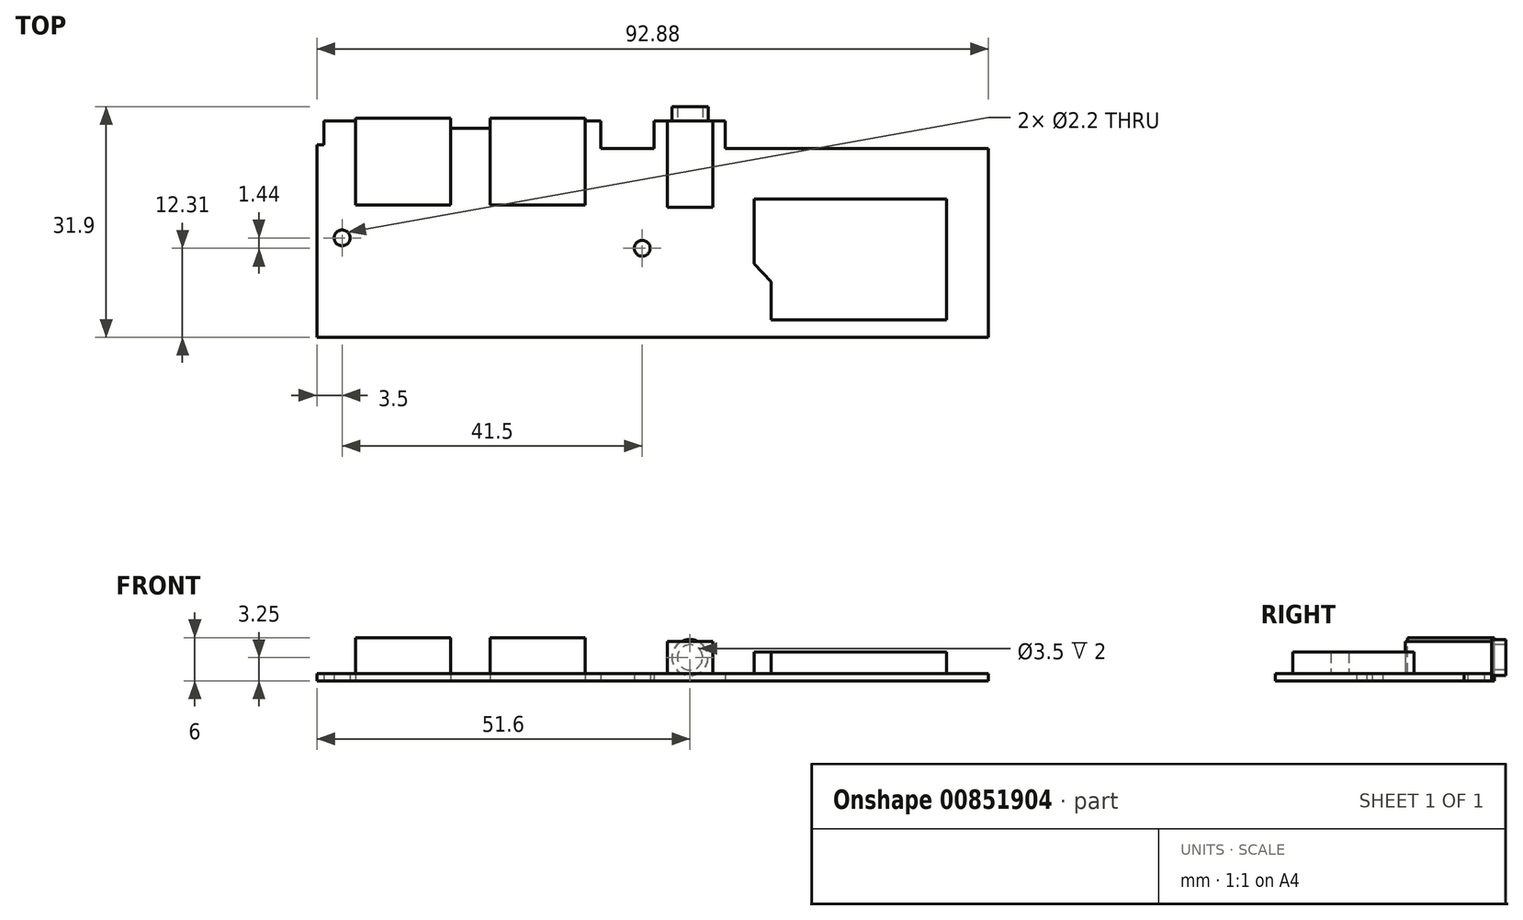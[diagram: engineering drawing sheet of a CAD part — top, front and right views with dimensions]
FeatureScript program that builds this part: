
annotation { "Feature Type Name" : "Feature", "Feature Type Description" : "" }
export const myFeature = defineFeature(function(context is Context, id is Id, definition is map)
    precondition{}
    {
        {
            var Q0;
            Q0=qCreatedBy(makeId("Top.planeOp"),FACE);
            var sketch = newSketch(context, id + "F0", { "sketchPlane" : qUnion([Q0])});
            skCircle(sketch, "E0", {"center": v(3.5, 13.75) * mm, "radius": 1.1 * mm});
            skCircle(sketch, "E1", {"center": v(45, 12.31) * mm, "radius": 1.1 * mm});
            skLineSegment(sketch, "E2", {"start": v(92.88, 26.1) * mm, "end": v(92.88, 0) * mm});
            skLineSegment(sketch, "E3", {"start": v(0, 0) * mm, "end": v(0, 26.6) * mm});
            skLineSegment(sketch, "E4", {"start": v(0, 26.6) * mm, "end": v(0.95, 26.6) * mm});
            skLineSegment(sketch, "E5", {"start": v(0.95, 26.6) * mm, "end": v(0.95, 29.9) * mm});
            skLineSegment(sketch, "E6", {"start": v(0.95, 29.9) * mm, "end": v(5.38, 29.9) * mm});
            skLineSegment(sketch, "E7", {"start": v(5.38, 29.9) * mm, "end": v(5.38, 18.3) * mm});
            skLineSegment(sketch, "E8", {"start": v(5.38, 18.3) * mm, "end": v(18.5, 18.3) * mm});
            skLineSegment(sketch, "E9", {"start": v(18.5, 18.3) * mm, "end": v(18.5, 28.9) * mm});
            skLineSegment(sketch, "E10", {"start": v(18.5, 28.9) * mm, "end": v(23.99, 28.9) * mm});
            skLineSegment(sketch, "E11", {"start": v(23.99, 28.9) * mm, "end": v(23.99, 18.3) * mm});
            skLineSegment(sketch, "E12", {"start": v(23.99, 18.3) * mm, "end": v(37.1, 18.3) * mm});
            skLineSegment(sketch, "E13", {"start": v(37.11, 18.3) * mm, "end": v(37.11, 29.9) * mm});
            skLineSegment(sketch, "E14", {"start": v(37.1, 29.9) * mm, "end": v(39.26, 29.9) * mm});
            skLineSegment(sketch, "E15", {"start": v(39.26, 29.9) * mm, "end": v(39.26, 26.1) * mm});
            skLineSegment(sketch, "E16", {"start": v(39.26, 26.1) * mm, "end": v(46.66, 26.1) * mm});
            skLineSegment(sketch, "E17", {"start": v(46.66, 26.1) * mm, "end": v(46.66, 29.9) * mm});
            skLineSegment(sketch, "E18", {"start": v(56.46, 29.9) * mm, "end": v(56.46, 26.1) * mm});
            skLineSegment(sketch, "E19", {"start": v(56.46, 26.1) * mm, "end": v(92.88, 26.1) * mm});
            skLineSegment(sketch, "E20", {"start": v(0, 0) * mm, "end": v(92.88, 0) * mm});
            skPoint(sketch, "E21", {"position": v(11.94, 18.3) * mm});
            skPoint(sketch, "E22", {"position": v(30.55, 18.3) * mm});
            skLineSegment(sketch, "E23", {"start": v(46.66, 29.9) * mm, "end": v(56.46, 29.9) * mm});
            skSolve(sketch);
        }
        {
            var Q0;
            Q0=makeQuery(id+"F0.imprint","IMPRINT",FACE,{"disambiguationData":[TD([[makeQuery(id+"F0.imprint","IMPRINT",EDGE,{"derivedFrom":sQuery(id+"F0.wireOp",EDGE,"E0")}),-1.0]])]});
            extrude(context, id + "F1", {"entities" : qUnion([Q0]), "depth" : 1 * mm, "offsetDistance" : 25 * mm});
        }
        {
            var Q0;
            Q0=makeQuery(id+"F1.opExtrude","CAP_FACE",FACE,{"disambiguationData":[OSD([sQuery(id+"F0.wireOp",EDGE,"E0"),sQuery(id+"F0.wireOp",EDGE,"E1"),sQuery(id+"F0.wireOp",EDGE,"E2"),sQuery(id+"F0.wireOp",EDGE,"E3"),sQuery(id+"F0.wireOp",EDGE,"E4"),sQuery(id+"F0.wireOp",EDGE,"E5"),sQuery(id+"F0.wireOp",EDGE,"E6"),sQuery(id+"F0.wireOp",EDGE,"E7"),sQuery(id+"F0.wireOp",EDGE,"E8"),sQuery(id+"F0.wireOp",EDGE,"E9"),sQuery(id+"F0.wireOp",EDGE,"E10"),sQuery(id+"F0.wireOp",EDGE,"E11"),sQuery(id+"F0.wireOp",EDGE,"E12"),sQuery(id+"F0.wireOp",EDGE,"E13"),sQuery(id+"F0.wireOp",EDGE,"E14"),sQuery(id+"F0.wireOp",EDGE,"E15"),sQuery(id+"F0.wireOp",EDGE,"E16"),sQuery(id+"F0.wireOp",EDGE,"E17"),sQuery(id+"F0.wireOp",EDGE,"E18"),sQuery(id+"F0.wireOp",EDGE,"E19"),sQuery(id+"F0.wireOp",EDGE,"E20"),sQuery(id+"F0.wireOp",EDGE,"E23")])],"isStart":false});
            var sketch = newSketch(context, id + "F2", { "sketchPlane" : qUnion([Q0])});
            skPoint(sketch, "E24.middle", {"position": v(51.6, 23.93) * mm});
            skLineSegment(sketch, "E25", {"start": v(87.1, 19.15) * mm, "end": v(87.1, 2.4) * mm});
            skLineSegment(sketch, "E26", {"start": v(87.1, 2.4) * mm, "end": v(62.8, 2.4) * mm});
            skLineSegment(sketch, "E27", {"start": v(62.8, 2.4) * mm, "end": v(62.8, 7.7) * mm});
            skLineSegment(sketch, "E28.bottom", {"start": v(54.75, 17.95) * mm, "end": v(48.45, 17.95) * mm});
            skLineSegment(sketch, "E28.top", {"start": v(54.75, 29.9) * mm, "end": v(48.45, 29.9) * mm});
            skLineSegment(sketch, "E28.left", {"start": v(54.75, 17.95) * mm, "end": v(54.75, 29.9) * mm});
            skLineSegment(sketch, "E28.right", {"start": v(48.45, 17.95) * mm, "end": v(48.45, 29.9) * mm});
            skLineSegment(sketch, "E29", {"start": v(87.1, 19.15) * mm, "end": v(60.5, 19.15) * mm});
            skLineSegment(sketch, "E30", {"start": v(60.5, 19.15) * mm, "end": v(60.5, 10.15) * mm});
            skLineSegment(sketch, "E31", {"start": v(60.5, 10.15) * mm, "end": v(62.8, 7.7) * mm});
            skSolve(sketch);
        }
        {
            var Q0;
            Q0=makeQuery(id+"F2.imprint","IMPRINT",FACE,{"disambiguationData":[TD([[makeQuery(id+"F2.imprint","IMPRINT",EDGE,{"derivedFrom":sQuery(id+"F2.wireOp",EDGE,"E28.bottom")}),-1.0]])]});
            extrude(context, id + "F3", {"entities" : qUnion([Q0]), "operationType" : NewBodyOperationType.ADD, "depth" : 4.5 * mm, "offsetDistance" : 25 * mm});
        }
        {
            var Q0;
            Q0=makeQuery(id+"F2.imprint","IMPRINT",FACE,{"disambiguationData":[TD([[makeQuery(id+"F2.imprint","IMPRINT",EDGE,{"derivedFrom":sQuery(id+"F2.wireOp",EDGE,"E25")}),-1.0]])]});
            extrude(context, id + "F4", {"entities" : qUnion([Q0]), "operationType" : NewBodyOperationType.ADD, "depth" : 3 * mm, "offsetDistance" : 25 * mm});
        }
        {
            var Q0;
            Q0=makeQuery(id+"F3.boolean.opBoolean","MERGE",FACE,{"derivedFrom":[makeQuery(id+"F1.opExtrude","SWEPT_FACE",FACE,{"disambiguationData":[OSD([sQuery(id+"F0.wireOp",EDGE,"E23")])]}),makeQuery(id+"F3.opExtrude","SWEPT_FACE",FACE,{"disambiguationData":[OSD([sQuery(id+"F2.wireOp",EDGE,"E28.top")])]})]});
            var sketch = newSketch(context, id + "F5", { "sketchPlane" : qUnion([Q0])});
            skCircle(sketch, "E32", {"center": v(-51.6, 3.25) * mm, "radius": 2.5 * mm});
            skPoint(sketch, "E32.centerSnap0", {"position": v(-48.45, 3.25) * mm});
            skPoint(sketch, "E32.centerSnap1", {"position": v(-51.6, 5.5) * mm});
            skCircle(sketch, "E33", {"center": v(-51.6, 3.25) * mm, "radius": 1.75 * mm});
            skSolve(sketch);
        }
        {
            var Q0;
            {var subQ0=sQuery(id+"F5.wireOp",EDGE,"E32");var subQ1=makeQuery(id+"F3.opExtrude","CAP_EDGE",EDGE,{"disambiguationData":[OSD([sQuery(id+"F2.wireOp",EDGE,"E28.top")])],"isStart":false});var subQ2=makeQuery(id+"F5.imprint","INTERSECT",VERTEX,{"disambiguationData":[OD(0.0)],"derivedFrom":[subQ1,subQ0]});Q0=makeQuery(id+"F5.imprint","IMPRINT",FACE,{"disambiguationData":[TD([[makeQuery(id+"F5.imprint","IMPRINT",EDGE,{"disambiguationData":[TD([[subQ2,1.0]])],"derivedFrom":subQ0}),1.0]])]});}
            var Q1;
            {var subQ0=sQuery(id+"F5.wireOp",EDGE,"E32");var subQ1=makeQuery(id+"F3.opExtrude","CAP_EDGE",EDGE,{"disambiguationData":[OSD([sQuery(id+"F2.wireOp",EDGE,"E28.top")])],"isStart":false});var subQ2=makeQuery(id+"F5.imprint","INTERSECT",VERTEX,{"disambiguationData":[OD(0.0)],"derivedFrom":[subQ1,subQ0]});Q1=makeQuery(id+"F5.imprint","IMPRINT",FACE,{"disambiguationData":[TD([[makeQuery(id+"F5.imprint","IMPRINT",EDGE,{"disambiguationData":[TD([[subQ2,-1.0]])],"derivedFrom":subQ0}),1.0]])]});}
            extrude(context, id + "F6", {"entities" : qUnion([Q0, Q1]), "operationType" : NewBodyOperationType.ADD, "depth" : 2 * mm, "offsetDistance" : 25 * mm});
        }
        {
            var Q0;
            Q0=makeQuery(id+"F1.opExtrude","SWEPT_FACE",FACE,{"disambiguationData":[OSD([sQuery(id+"F0.wireOp",EDGE,"E8")])]});
            var sketch = newSketch(context, id + "F7", { "sketchPlane" : qUnion([Q0])});
            skLineSegment(sketch, "E34.bottom", {"start": v(-18.5, 0) * mm, "end": v(-5.38, 0) * mm});
            skLineSegment(sketch, "E34.top", {"start": v(-18.5, 6) * mm, "end": v(-5.38, 6) * mm});
            skLineSegment(sketch, "E34.left", {"start": v(-18.5, 0) * mm, "end": v(-18.5, 6) * mm});
            skLineSegment(sketch, "E34.right", {"start": v(-5.38, 0) * mm, "end": v(-5.38, 6) * mm});
            skPoint(sketch, "E34.middle", {"position": v(-11.94, 3) * mm});
            skPoint(sketch, "E34.middle.positionSnap0", {"position": v(-11.94, 0) * mm});
            skPoint(sketch, "E34.centerSnap0", {"position": v(-11.94, 0) * mm});
            skSolve(sketch);
        }
        {
            var Q0;
            {var subQ0=sQuery(id+"F7.wireOp",EDGE,"E34.top");Q0=makeQuery(id+"F7.imprint","IMPRINT",FACE,{"disambiguationData":[TD([[makeQuery(id+"F7.imprint","IMPRINT",EDGE,{"derivedFrom":subQ0}),-1.0]])]});}
            var Q1;
            {var subQ0=sQuery(id+"F7.wireOp",EDGE,"E34.bottom");Q1=makeQuery(id+"F7.imprint","IMPRINT",FACE,{"disambiguationData":[TD([[makeQuery(id+"F7.imprint","IMPRINT",EDGE,{"derivedFrom":subQ0}),-1.0]])]});}
            extrude(context, id + "F8", {"entities" : qUnion([Q0, Q1]), "operationType" : NewBodyOperationType.ADD, "depth" : 12 * mm, "offsetDistance" : 25 * mm});
        }
        {
            var Q0;
            Q0=makeQuery(id+"F1.opExtrude","SWEPT_FACE",FACE,{"disambiguationData":[OSD([sQuery(id+"F0.wireOp",EDGE,"E12")])]});
            var sketch = newSketch(context, id + "F9", { "sketchPlane" : qUnion([Q0])});
            skLineSegment(sketch, "E35.bottom", {"start": v(-37.1, 0) * mm, "end": v(-23.99, 0) * mm});
            skLineSegment(sketch, "E35.top", {"start": v(-37.1, 6) * mm, "end": v(-23.99, 6) * mm});
            skLineSegment(sketch, "E35.left", {"start": v(-37.1, 0) * mm, "end": v(-37.1, 6) * mm});
            skLineSegment(sketch, "E35.right", {"start": v(-23.99, 0) * mm, "end": v(-23.99, 6) * mm});
            skPoint(sketch, "E35.middle", {"position": v(-30.55, 3) * mm});
            skPoint(sketch, "E35.middle.positionSnap0", {"position": v(-30.55, 0) * mm});
            skPoint(sketch, "E35.centerSnap0", {"position": v(-30.55, 0) * mm});
            skSolve(sketch);
        }
        {
            var Q0;
            {var subQ0=sQuery(id+"F9.wireOp",EDGE,"E35.top");Q0=makeQuery(id+"F9.imprint","IMPRINT",FACE,{"disambiguationData":[TD([[makeQuery(id+"F9.imprint","IMPRINT",EDGE,{"derivedFrom":subQ0}),-1.0]])]});}
            var Q1;
            {var subQ0=sQuery(id+"F9.wireOp",EDGE,"E35.bottom");Q1=makeQuery(id+"F9.imprint","IMPRINT",FACE,{"disambiguationData":[TD([[makeQuery(id+"F9.imprint","IMPRINT",EDGE,{"derivedFrom":subQ0}),-1.0]])]});}
            extrude(context, id + "F10", {"entities" : qUnion([Q0, Q1]), "operationType" : NewBodyOperationType.ADD, "depth" : 12 * mm, "offsetDistance" : 25 * mm});
        }
    });
